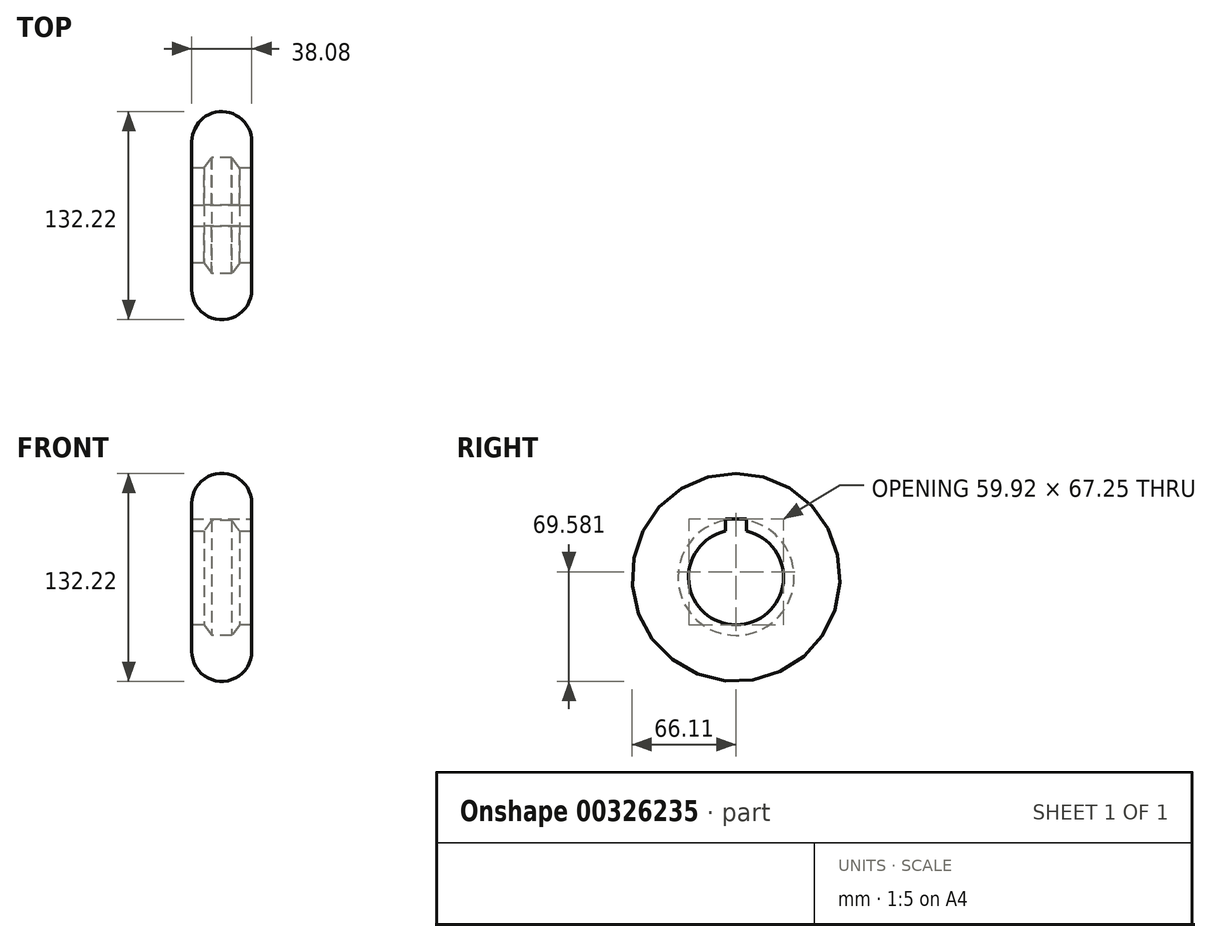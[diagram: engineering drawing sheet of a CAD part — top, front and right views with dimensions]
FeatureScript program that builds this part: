
annotation { "Feature Type Name" : "Feature", "Feature Type Description" : "" }
export const myFeature = defineFeature(function(context is Context, id is Id, definition is map)
    precondition{}
    {
        {
            var Q0;
            Q0=qCreatedBy(makeId("Front.planeOp"),FACE);
            var sketch = newSketch(context, id + "F0", { "sketchPlane" : qUnion([Q0])});
            skLineSegment(sketch, "E0", {"start": v(-75.93, 0) * mm, "end": v(75.1, 0) * mm});
            skLineSegment(sketch, "E1", {"start": v(19.04, 30.15) * mm, "end": v(11.22, 30.15) * mm});
            skLineSegment(sketch, "E2", {"start": v(-19.04, 30.15) * mm, "end": v(-19.04, 47.07) * mm});
            skLineSegment(sketch, "E3", {"start": v(19.04, 47.07) * mm, "end": v(19.04, 30.15) * mm});
            skPoint(sketch, "E4", {"position": v(0, 30.15) * mm});
            skArc(sketch, "E5", {"start": v(19.04, 47.07) * mm, "mid": v(0, 66.1) * mm, "end": v(-19.04, 47.07) * mm});
            skLineSegment(sketch, "E6", {"start": v(-11.22, 30.15) * mm, "end": v(-6.37, 36.87) * mm});
            skLineSegment(sketch, "E7", {"start": v(-6.37, 36.87) * mm, "end": v(6.37, 36.87) * mm});
            skLineSegment(sketch, "E8", {"start": v(6.37, 36.87) * mm, "end": v(11.22, 30.15) * mm});
            skPoint(sketch, "E9", {"position": v(0, 36.87) * mm});
            skPoint(sketch, "E9.positionSnap0", {"position": v(0, 36.87) * mm});
            skLineSegment(sketch, "E10.trimOffspring", {"start": v(0, 30.15) * mm, "end": v(0, 30.15) * mm});
            skLineSegment(sketch, "E11.trimOffspring", {"start": v(-11.22, 30.15) * mm, "end": v(-19.04, 30.15) * mm});
            skSolve(sketch);
        }
        {
            var Q0;
            Q0=makeQuery(id+"F0.imprint","IMPRINT",FACE,{"disambiguationData":[TD([[makeQuery(id+"F0.imprint","IMPRINT",EDGE,{"derivedFrom":sQuery(id+"F0.wireOp",EDGE,"E1")}),-1.0]])]});
            var Q1;
            Q1=sQuery(id+"F0.wireOp",EDGE,"E0");
            revolve(context, id + "F1", {"entities" : qUnion([Q0]), "axis" : qUnion([Q1]), "revolveType" : RevolveType.FULL});
        }
        {
            var Q0;
            Q0=makeQuery(id+"F1.opRevolve","SWEPT_FACE",FACE,{"disambiguationData":[OSD([sQuery(id+"F0.wireOp",EDGE,"E3")])]});
            var sketch = newSketch(context, id + "F2", { "sketchPlane" : qUnion([Q0])});
            skLineSegment(sketch, "E12.bottom", {"start": v(-6.73, 23.2) * mm, "end": v(6.73, 23.2) * mm});
            skLineSegment(sketch, "E12.top", {"start": v(-6.73, 37.1) * mm, "end": v(6.73, 37.1) * mm});
            skLineSegment(sketch, "E12.left", {"start": v(-6.73, 23.2) * mm, "end": v(-6.73, 37.1) * mm});
            skLineSegment(sketch, "E12.right", {"start": v(6.73, 23.2) * mm, "end": v(6.73, 37.1) * mm});
            skPoint(sketch, "E12.middle", {"position": v(0, 30.15) * mm});
            skSolve(sketch);
        }
        {
            var Q0;
            {var subQ0=sQuery(id+"F2.wireOp",EDGE,"E12.top");Q0=makeQuery(id+"F2.imprint","IMPRINT",FACE,{"disambiguationData":[TD([[makeQuery(id+"F2.imprint","IMPRINT",EDGE,{"derivedFrom":subQ0}),-1.0]])]});}
            extrude(context, id + "F3", {"entities" : qUnion([Q0]), "operationType" : NewBodyOperationType.REMOVE, "endBound" : BoundingType.THROUGH_ALL, "oppositeDirection" : true, "depth" : 25.4 * mm});
        }
    });
